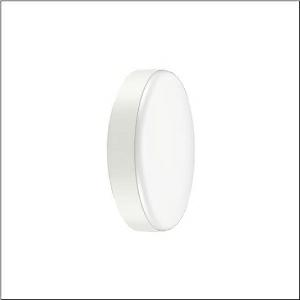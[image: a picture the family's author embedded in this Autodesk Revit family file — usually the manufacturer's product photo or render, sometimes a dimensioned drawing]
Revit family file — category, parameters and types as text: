
# Revit family: round_31_51wc10mb34as
name_source: partatom
category: Lighting Fixtures
units: mm (PartAtom-declared; Revit-internal decimal feet)

## family parameters
Cut with Voids When Loaded = No
Host = Face
Light Source = No
Part Type = Normal
Room Calculation Point = No
Round Connector Dimension = Use Diameter
Shared = No

## types (1)
- --- (1 x LED, 4250 lm, 35.4 W, 3000K)
    Apparent Load = 35 VA
    CIE Flux Codes = 44 75 94 94 100
    Color Rendering = 80
    Color Temperature = 3000K
    Default Elevation = 1800 mm
    Description = Round 31, wall and ceiling luminaire, primary optical cover: cover, of PC, opal, light emission: direct distribution, primary light characteristic: symmetric, installation type: surface-mounted, LED, rated luminous flux: 4.250lm, luminous efficacy: 120lm/W, light colour: 830, colour temperature: 3000K, control gear: ON/OFF Multilumen, with terminal, 3-pole, max. 2.5mm², mains connection: 220..240V, AC, 50/60Hz, rated input power: 35W, luminaire housing, of PC, traffic white (RAL 9016), diameter: 480mm, brightness and presence sensor, HF sensor, protection rating (complete): IP65, insulation class (complete): insulation class II (safety insulation), certification: CE, impact resistance: IK10, permissible operating ambient temperature: -20..+40°C, permissible storage temperature: -20..+60°C, packaging unit: 1 piece
    Height = 97 mm
    Lamp = 1 x LED
    Lamp Light Flux = 4250 lm
    Lamp Power = 35.4 W
    Lamp count = 1
    Length = 480 mm
    Luminous efficacy = 120 lm/W
    Manufacturer = Siteco
    ModVariant = No
    Model = 51WC10MB34AS
    Mounting Place = Wall
    Mounting Type = Surface mounted
    Number of Poles = 1
    OnlyDefault = Yes
    Power Factor = 1
    Product Name = Round 31
    Product group = wall and ceiling luminaire | wall mounted
    ProductGroupID = 2001
    Protection Class = Protection class II
    Protection Degree = IP 65
    RLX_Detail_Level = 1
    RLX_Emergency_Light_Flux = 0 lm
    RLX_Emergency_Type = 0
    RLX_Emergency_Type_DB = No
    RlxData = <blob elided: 41529 chars, md5=102ce3fb>
    Socket = socket
    Standby Power = 0 W
    System Light Flux = 4250 lm
    System Power = 35 W
    Type Comments = factory setting: luminous flux: 100 % | (ON | ON)
    Type Image = l_1007188.jpg
    URL = http://relux.com
    VarID = @adj_111797
    Voltage = 0 V
    Weight = 0.00 kg
    Width = 0 mm  [stored 0 ft]

note: [stored X ft] marks values corroborated as IEEE doubles in the binary element streams (Revit-internal decimal feet)

## geometry (parser evidence)
native form markers: Blend x4, Sweep x12
no freeform markers — native parametric forms only
